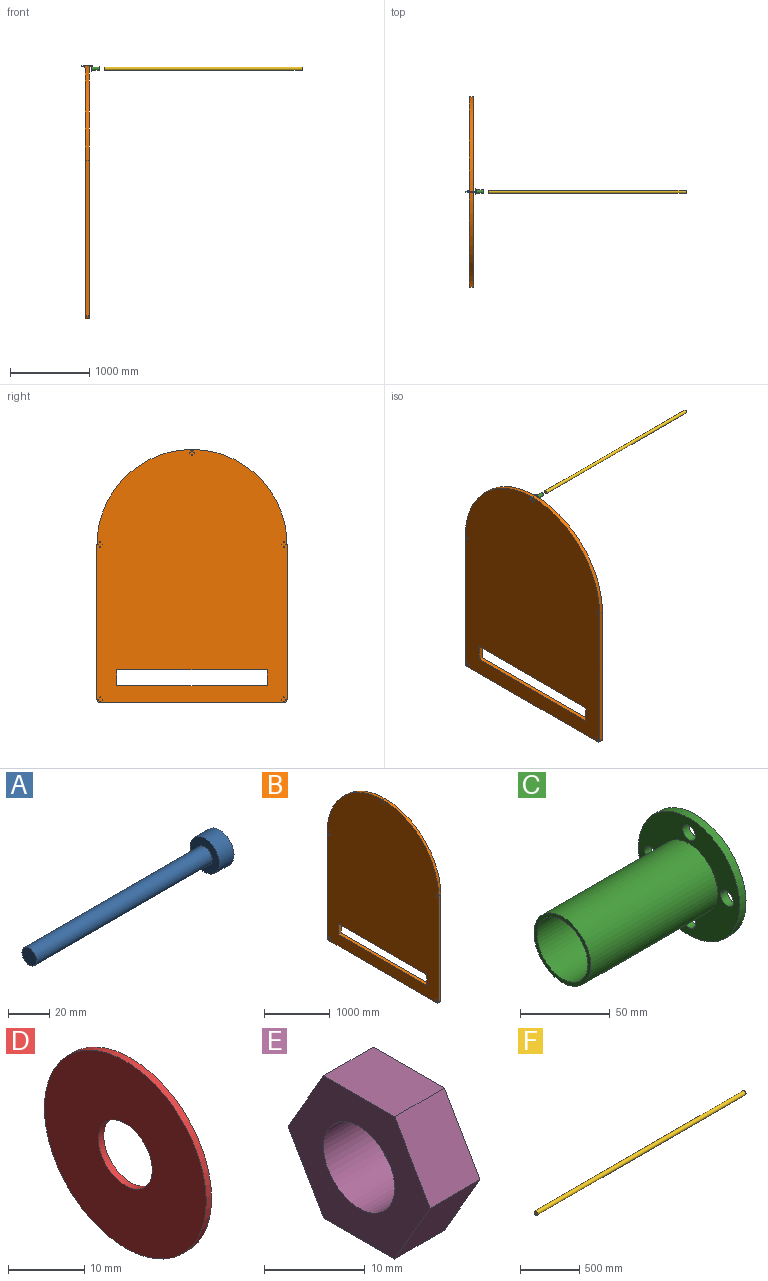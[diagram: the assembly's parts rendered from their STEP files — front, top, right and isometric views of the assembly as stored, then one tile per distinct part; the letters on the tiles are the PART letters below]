
ASSEMBLY  parts=6 mates=9
PART A: 5 faces, bbox 130x20x20 mm
  f0: cylinder r=10mm len=20mm, axis (-1,0,0), area 628.3mm2, adj f1,f2
  f1: plane 20x20mm, normal (1,0,0), area 314.2mm2, adj f0
  f2: plane 20x20mm, normal (-1,0,0), area 235.6mm2, adj f0,f3
  f3: cylinder r=5mm len=120mm, axis (1,0,0), area 3769.9mm2, adj f2,f4
  f4: plane 10x10mm, normal (-1,0,0), area 78.5mm2, adj f3
PART B: 32 faces, bbox 50x2400x3200 mm
  f0: plane 1960x50mm, normal (0,1,0), area 98000mm2, adj f1,f27,f30,f31
  f1: cylinder r=1200mm len=2400mm, axis (1,0,0), area 188495.6mm2, adj f0,f2,f30,f31
  f2: plane 1960x50mm, normal (0,-1,0), area 98000mm2, adj f1,f3,f30,f31
  f3: cylinder r=40mm len=50mm, axis (1,0,0), area 3141.6mm2, adj f2,f4,f30,f31
  f4: plane 2320x50mm, normal (0,0,-1), area 116000mm2, adj f3,f27,f30,f31
  f5: plane 200x50mm, normal (0,1,0), area 10000mm2, adj f6,f28,f30,f31
  f6: plane 1900x50mm, normal (0,0,-1), area 95000mm2, adj f5,f7,f30,f31
  f7: plane 200x50mm, normal (0,-1,0), area 10000mm2, adj f6,f28,f30,f31
  f8: cylinder r=5mm len=50mm, axis (1,0,0), area 1570.8mm2, adj f30,f31
  f9: cylinder r=5mm len=50mm, axis (1,0,0), area 1570.8mm2, adj f30,f31
  f10: cylinder r=5mm len=50mm, axis (1,0,0), area 1570.8mm2, adj f30,f31
  f11: cylinder r=5mm len=50mm, axis (1,0,0), area 1570.8mm2, adj f30,f31
  f12: cylinder r=5mm len=50mm, axis (1,0,0), area 1570.8mm2, adj f30,f31
  f13: cylinder r=5mm len=50mm, axis (1,0,0), area 1570.8mm2, adj f30,f31
  f14: cylinder r=5mm len=50mm, axis (1,0,0), area 1570.8mm2, adj f30,f31
  f15: cylinder r=5mm len=50mm, axis (1,0,0), area 1570.8mm2, adj f30,f31
  f16: cylinder r=5mm len=50mm, axis (1,0,0), area 1570.8mm2, adj f30,f31
  f17: cylinder r=5mm len=50mm, axis (1,0,0), area 1570.8mm2, adj f30,f31
  f18: cylinder r=5mm len=50mm, axis (1,0,0), area 1570.8mm2, adj f30,f31
  f19: cylinder r=5mm len=50mm, axis (1,0,0), area 1570.8mm2, adj f30,f31
  f20: cylinder r=5mm len=50mm, axis (1,0,0), area 1570.8mm2, adj f30,f31
  f21: cylinder r=5mm len=50mm, axis (1,0,0), area 1570.8mm2, adj f30,f31
  f22: cylinder r=5mm len=50mm, axis (1,0,0), area 1570.8mm2, adj f30,f31
  f23: cylinder r=5mm len=50mm, axis (1,0,0), area 1570.8mm2, adj f30,f31
  f24: cylinder r=5mm len=50mm, axis (1,0,0), area 1570.8mm2, adj f30,f31
  f25: cylinder r=5mm len=50mm, axis (1,0,0), area 1570.8mm2, adj f30,f31
  f26: cylinder r=5mm len=50mm, axis (1,0,0), area 1570.8mm2, adj f30,f31
  f27: cylinder r=40mm len=50mm, axis (1,0,0), area 3141.6mm2, adj f0,f4,f30,f31
  f28: plane 1900x50mm, normal (0,0,1), area 95000mm2, adj f5,f7,f30,f31
  f29: cylinder r=5mm len=50mm, axis (1,0,0), area 1570.8mm2, adj f30,f31
  f30: plane 3200x2400mm, normal (-1,0,0), area 6679689.2mm2, adj f0,f1,f2,f3,f4,f5,f6,f7
  f31: plane 3200x2400mm, normal (1,0,0), area 6679689.2mm2, adj f0,f1,f2,f3,f4,f5,f6,f7
PART C: 11 faces, bbox 105x80x80 mm
  f0: cylinder r=40mm len=80mm, axis (1,0,0), area 1256.6mm2, adj f1,f2
  f1: plane 80x80mm, normal (-1,0,0), area 3122mm2, adj f0,f4,f7,f8,f9,f10
  f2: plane 80x80mm, normal (1,0,0), area 4712.4mm2, adj f0,f7,f8,f9,f10
  f3: cylinder r=20mm len=100mm, axis (1,0,0), area 12566.4mm2, adj f5,f6
  f4: cylinder r=22.5mm len=100mm, axis (1,0,0), area 14137.2mm2, adj f1,f5
  f5: plane 45x45mm, normal (-1,0,0), area 333.8mm2, adj f3,f4
  f6: plane 40x40mm, normal (-1,0,0), area 1256.6mm2, adj f3
  f7: cylinder r=5mm len=10mm, axis (1,0,0), area 157.1mm2, adj f1,f2
  f8: cylinder r=5mm len=10mm, axis (1,0,0), area 157.1mm2, adj f1,f2
  f9: cylinder r=5mm len=10mm, axis (1,0,0), area 157.1mm2, adj f1,f2
  f10: cylinder r=5mm len=10mm, axis (1,0,0), area 157.1mm2, adj f1,f2
PART D: 4 faces, bbox 1x30x30 mm
  f0: cylinder r=15mm len=30mm, axis (-1,0,0), area 94.2mm2, adj f1,f2
  f1: plane 30x30mm, normal (1,0,0), area 628.3mm2, adj f0,f3
  f2: plane 30x30mm, normal (-1,0,0), area 628.3mm2, adj f0,f3
  f3: cylinder r=5mm len=10mm, axis (1,0,0), area 31.4mm2, adj f1,f2
PART E: 9 faces, bbox 7x20x17.3 mm
  f0: plane 10x7mm, normal (0,0,-1), area 70mm2, adj f1,f5,f6,f7
  f1: plane 8.66x7mm, normal (0,0.87,-0.5), area 70mm2, adj f0,f2,f6,f7
  f2: plane 8.66x7mm, normal (0,0.87,0.5), area 70mm2, adj f1,f3,f6,f7
  f3: plane 10x7mm, normal (0,0,1), area 70mm2, adj f2,f4,f6,f7
  f4: plane 8.66x7mm, normal (0,-0.87,0.5), area 70mm2, adj f3,f5,f6,f7
  f5: plane 8.66x7mm, normal (0,-0.87,-0.5), area 70mm2, adj f0,f4,f6,f7
  f6: plane 20x17.32mm, normal (1,0,0), area 181.3mm2, adj f0,f1,f2,f3,f4,f5,f8
  f7: plane 20x17.32mm, normal (-1,0,0), area 181.3mm2, adj f0,f1,f2,f3,f4,f5,f8
  f8: cylinder r=5mm len=10mm, axis (1,0,0), area 219.9mm2, adj f6,f7
PART F: 3 faces, bbox 2500x40x40 mm
  f0: cylinder r=20mm len=2500mm, axis (-1,0,0), area 314159.3mm2, adj f1,f2
  f1: plane 40x40mm, normal (1,0,0), area 1256.6mm2, adj f0
  f2: plane 40x40mm, normal (-1,0,0), area 1256.6mm2, adj f0
PLACE A t=(5,1217.1,3210.11)mm
PLACE B t=(-21.86,17.1,20.11)mm
PLACE C rot(axis=(0,1,0),180deg) t=(0,1217.1,3180.11)mm
PLACE D t=(-82.96,1217.1,3210.11)mm
PLACE E t=(-93.67,1217.1,3210.11)mm
PLACE F t=(164.35,1217.1,3180.11)mm
MATE slider E.f8 <-> D.f3  axis (1,0,0) through (-86.67,1217.1,3210.11)mm
MATE slider C.f9 <-> B.f14  axis (-1,0,0) through (0,1217.1,3210.11)mm
MATE slider A.f0 <-> C.f9  axis (-1,0,0) through (5,1217.1,3210.11)mm
MATE slider C.f10 <-> B.f11  axis (-1,0,0) through (0,1187.1,3180.11)mm
MATE slider D.f3 <-> E.f8  axis (-1,0,0) through (-82.96,1217.1,3210.11)mm
MATE slider F.f0 <-> C.f3  axis (-1,0,0) through (164.35,1217.1,3180.11)mm
MATE slider D.f3 <-> B.f14  axis (1,0,0) through (-81.96,1217.1,3210.11)mm
MATE slider B.f14 <-> D.f0  axis (-1,0,0) through (-71.86,1217.1,3210.11)mm
MATE slider A.f3 <-> C.f9  axis (1,0,0) through (-115,1217.1,3210.11)mm
